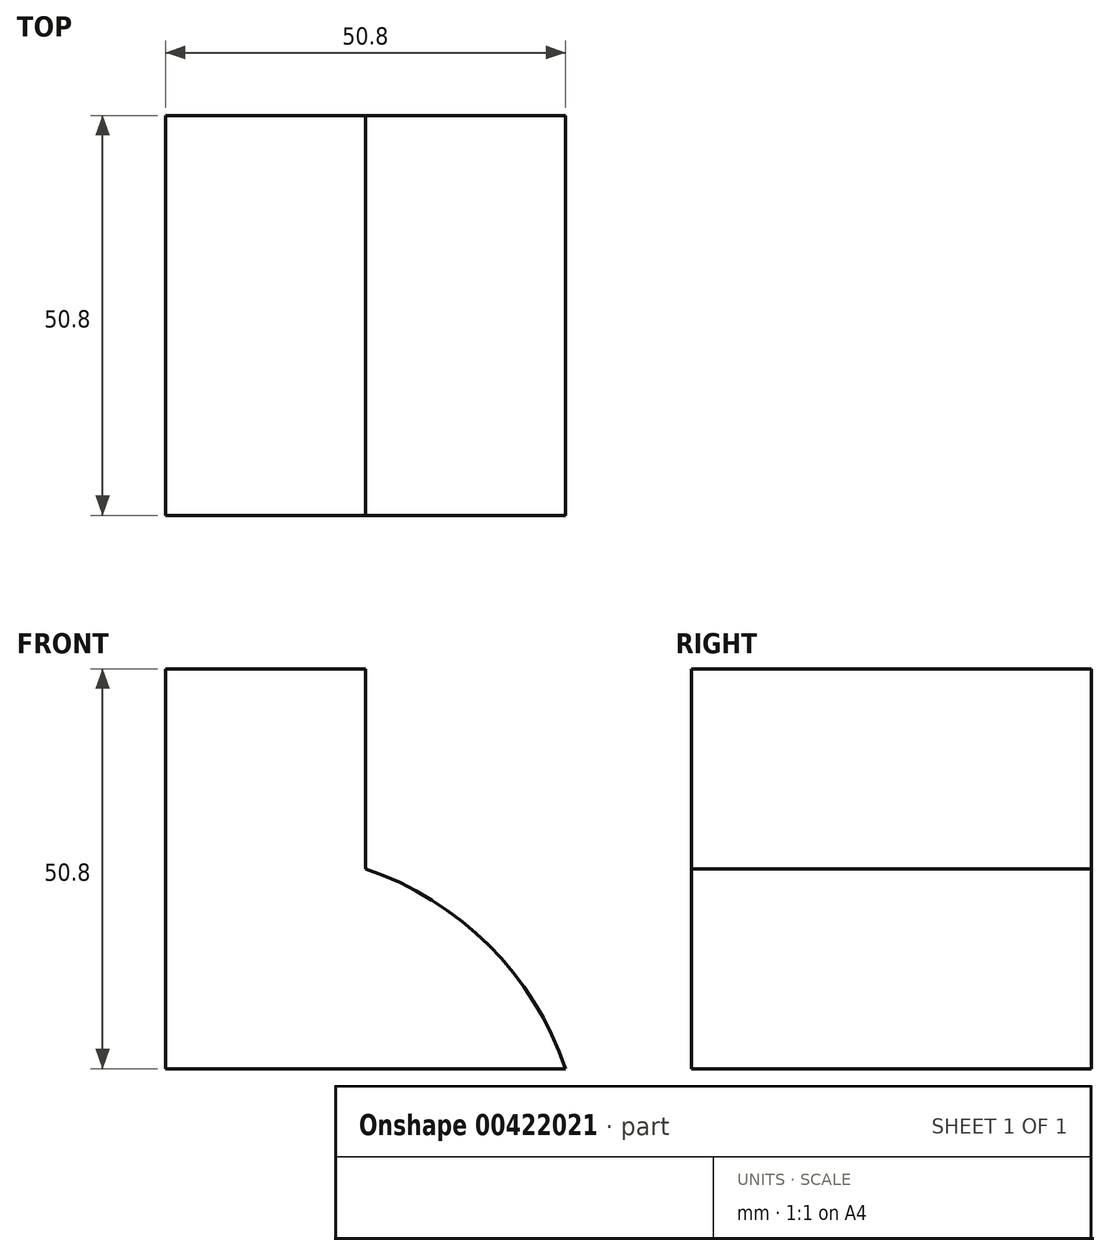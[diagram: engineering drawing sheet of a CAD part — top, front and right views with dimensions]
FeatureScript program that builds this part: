
annotation { "Feature Type Name" : "Feature", "Feature Type Description" : "" }
export const myFeature = defineFeature(function(context is Context, id is Id, definition is map)
    precondition{}
    {
        {
            var Q0;
            Q0=qCreatedBy(makeId("Front.planeOp"),FACE);
            var sketch = newSketch(context, id + "F0", { "sketchPlane" : qUnion([Q0])});
            skLineSegment(sketch, "E0", {"start": v(-50.8, 0) * mm, "end": v(0, 0) * mm});
            skLineSegment(sketch, "E1", {"start": v(-50.8, 0) * mm, "end": v(-50.8, 50.8) * mm});
            skLineSegment(sketch, "E2", {"start": v(-50.8, 50.8) * mm, "end": v(-25.4, 50.8) * mm});
            skLineSegment(sketch, "E3", {"start": v(-25.4, 50.8) * mm, "end": v(-25.4, 25.4) * mm});
            skArc(sketch, "E4", {"start": v(0, 0) * mm, "mid": v(-9.73, 15.67) * mm, "end": v(-25.4, 25.4) * mm});
            skSolve(sketch);
        }
        {
            var Q0;
            Q0 = qSketchRegion(id + "F0", true);
            extrude(context, id + "F1", {"entities" : qUnion([Q0]), "depth" : 50.8 * mm});
        }
    });
